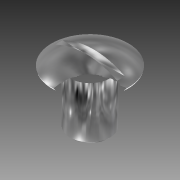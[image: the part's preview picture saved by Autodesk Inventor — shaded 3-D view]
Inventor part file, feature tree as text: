
AUTODESK INVENTOR PART (.ipt)
format: ipt  version: 2014 (Build 180170000, 170)  size: 110,592 bytes
history: native  units: mm (DEFAULTED — no unit token found)
features: sketch x2, revolve x1, chamfer x1, extrude x1
ambient origin geometry x8: Origin, YZ Plane, XZ Plane, XY Plane, X Axis, Y Axis, Z Axis, Center Point
bodies: Solid1 (feature_tree)
feature tree (5):
  revolve  "Revolution1"  [1 undecoded]
  chamfer  "Chamfer1"  Angle=90.0deg  [1 undecoded]
  extrude  "Extrusion1"  Depth=0.127mm
  sketch  "Sketch1"  dims[d1=1.190625mm d2=2.38125mm]
  sketch  "Sketch2"  dims[d3=0.79375mm d4=90.0deg d5=0.127mm d6=0.127mm d7=25.4mm d8=0.0mm d9=45.0deg]
note: 2 required parameter values undecoded (feature->parameter linkage not recoverable at this tier; creation-order binding heuristic only, values carry confidence <= 0.55)